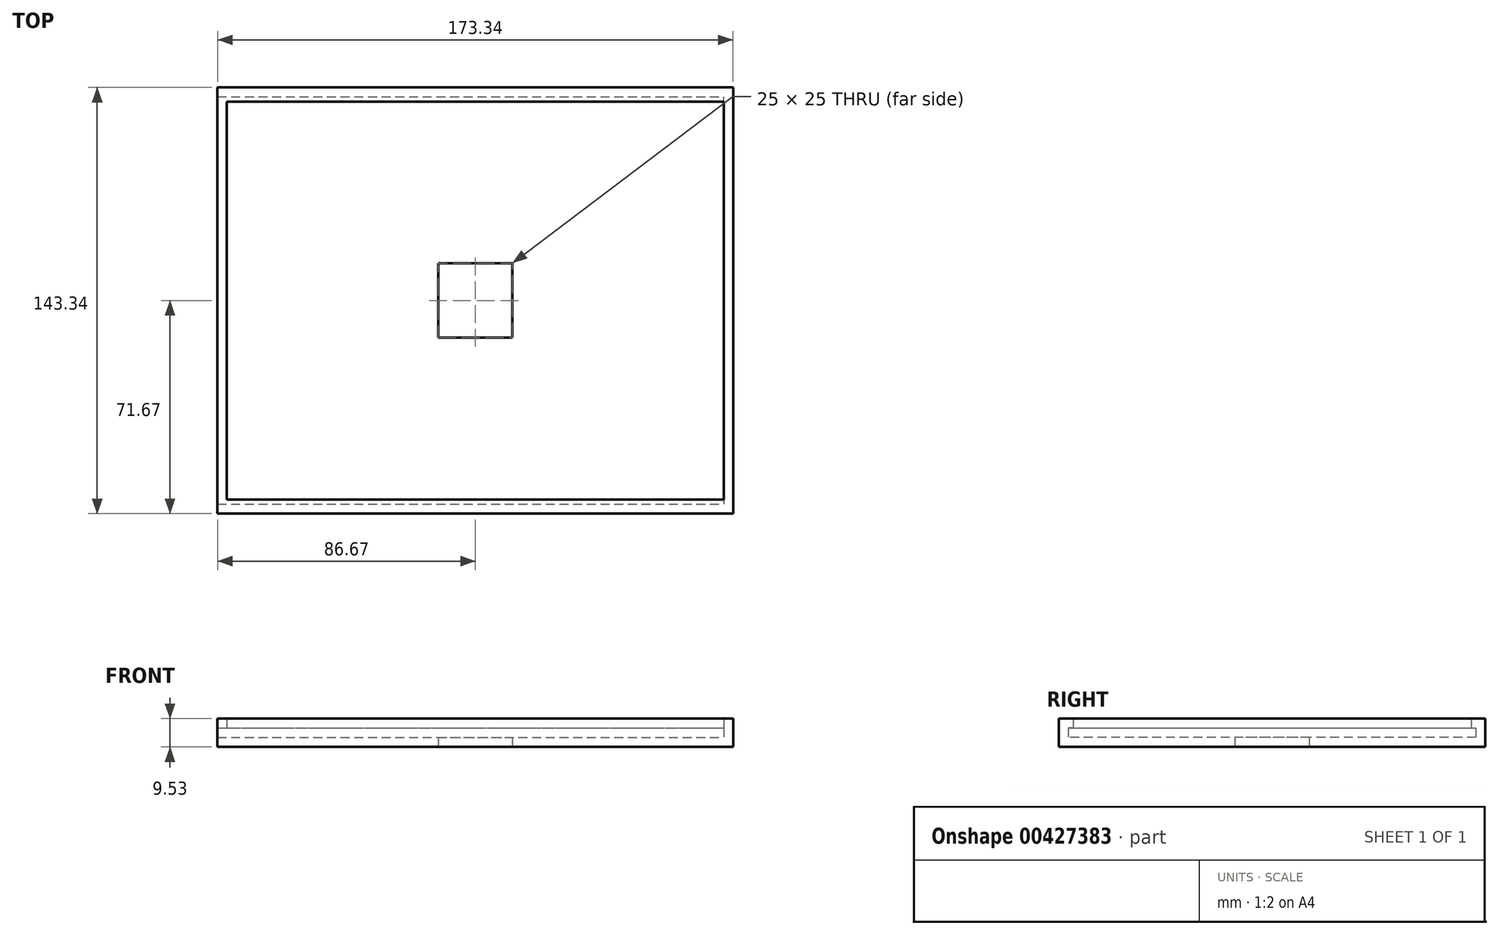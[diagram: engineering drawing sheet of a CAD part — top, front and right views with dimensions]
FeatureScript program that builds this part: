
annotation { "Feature Type Name" : "Feature", "Feature Type Description" : "" }
export const myFeature = defineFeature(function(context is Context, id is Id, definition is map)
    precondition{}
    {
        {
            var Q0;
            Q0=qCreatedBy(makeId("Top.planeOp"),FACE);
            var sketch = newSketch(context, id + "F0", { "sketchPlane" : qUnion([Q0])});
            skPoint(sketch, "E0.middle", {"position": v(0, 0) * mm});
            skLineSegment(sketch, "E1.bottom", {"start": v(-67.1, 68.5) * mm, "end": v(-41.7, 68.5) * mm});
            skLineSegment(sketch, "E1.top", {"start": v(-67.1, -68.5) * mm, "end": v(-41.7, -68.5) * mm});
            skLineSegment(sketch, "E1.left", {"start": v(-83.5, 52.1) * mm, "end": v(-83.5, 26.7) * mm});
            skLineSegment(sketch, "E1.right", {"start": v(83.5, 52.1) * mm, "end": v(83.5, 26.7) * mm});
            skLineSegment(sketch, "E2.bottom", {"start": v(-12.5, 12.5) * mm, "end": v(12.5, 12.5) * mm});
            skLineSegment(sketch, "E2.top", {"start": v(-12.5, -12.5) * mm, "end": v(12.5, -12.5) * mm});
            skLineSegment(sketch, "E2.left", {"start": v(-12.5, 12.5) * mm, "end": v(-12.5, -12.5) * mm});
            skLineSegment(sketch, "E2.right", {"start": v(12.5, 12.5) * mm, "end": v(12.5, -12.5) * mm});
            skLineSegment(sketch, "E3.trimOffspring", {"start": v(-83.5, -24.1) * mm, "end": v(-83.5, -49.5) * mm});
            skLineSegment(sketch, "E4.trimOffspring", {"start": v(34.5, -68.5) * mm, "end": v(59.9, -68.5) * mm});
            skLineSegment(sketch, "E5.trimOffspring", {"start": v(83.5, -24.1) * mm, "end": v(83.5, -49.5) * mm});
            skLineSegment(sketch, "E6.trimOffspring", {"start": v(34.5, 68.5) * mm, "end": v(59.9, 68.5) * mm});
            skLineSegment(sketch, "E7.trimOffspring", {"start": v(-16.3, 68.5) * mm, "end": v(9.1, 68.5) * mm});
            skLineSegment(sketch, "E8", {"start": v(-16.3, -68.5) * mm, "end": v(9.1, -68.5) * mm});
            skLineSegment(sketch, "E9", {"start": v(-83.5, 52.1) * mm, "end": v(-83.5, 68.5) * mm});
            skLineSegment(sketch, "E10", {"start": v(-83.5, 68.5) * mm, "end": v(-67.1, 68.5) * mm});
            skLineSegment(sketch, "E11", {"start": v(-41.7, 68.5) * mm, "end": v(-16.3, 68.5) * mm});
            skLineSegment(sketch, "E12", {"start": v(9.1, 68.5) * mm, "end": v(34.5, 68.5) * mm});
            skLineSegment(sketch, "E13", {"start": v(59.9, 68.5) * mm, "end": v(83.5, 68.5) * mm});
            skLineSegment(sketch, "E14", {"start": v(83.5, 68.5) * mm, "end": v(83.5, 52.1) * mm});
            skLineSegment(sketch, "E15", {"start": v(83.5, -24.1) * mm, "end": v(83.5, 26.7) * mm});
            skLineSegment(sketch, "E16", {"start": v(83.5, -49.5) * mm, "end": v(83.5, -68.5) * mm});
            skLineSegment(sketch, "E17", {"start": v(83.5, -68.5) * mm, "end": v(59.9, -68.5) * mm});
            skLineSegment(sketch, "E18", {"start": v(34.5, -68.5) * mm, "end": v(9.1, -68.5) * mm});
            skLineSegment(sketch, "E19", {"start": v(-16.3, -68.5) * mm, "end": v(-41.7, -68.5) * mm});
            skLineSegment(sketch, "E20", {"start": v(-83.5, -49.5) * mm, "end": v(-83.5, -68.5) * mm});
            skLineSegment(sketch, "E21", {"start": v(-83.5, -68.5) * mm, "end": v(-67.1, -68.5) * mm});
            skLineSegment(sketch, "E22", {"start": v(-83.5, -24.1) * mm, "end": v(-83.5, 26.7) * mm});
            skLineSegment(sketch, "E23.bottom", {"start": v(-86.68, 71.67) * mm, "end": v(86.68, 71.67) * mm});
            skLineSegment(sketch, "E23.top", {"start": v(-86.68, -71.67) * mm, "end": v(86.68, -71.67) * mm});
            skLineSegment(sketch, "E23.left", {"start": v(-86.68, 71.67) * mm, "end": v(-86.68, -71.67) * mm});
            skLineSegment(sketch, "E23.right", {"start": v(86.68, 71.67) * mm, "end": v(86.68, -71.67) * mm});
            skSolve(sketch);
        }
        {
            var Q0;
            Q0=makeQuery(id+"F0.imprint","IMPRINT",FACE,{"disambiguationData":[TD([[makeQuery(id+"F0.imprint","IMPRINT",EDGE,{"derivedFrom":sQuery(id+"F0.wireOp",EDGE,"E1.bottom")}),-1.0]])]});
            extrude(context, id + "F1", {"entities" : qUnion([Q0]), "depth" : 3.17 * mm, "offsetDistance" : 25.4 * mm});
        }
        {
            var Q0;
            Q0 = qSketchRegion(id + "F0", true);
            extrude(context, id + "F2", {"entities" : qUnion([Q0]), "operationType" : NewBodyOperationType.ADD, "depth" : 9.52 * mm});
        }
        {
            var Q0;
            Q0=makeQuery(id+"F2.opExtrude","SWEPT_FACE",FACE,{"disambiguationData":[OSD([sQuery(id+"F0.wireOp",EDGE,"E1.left"),sQuery(id+"F0.wireOp",EDGE,"E3.trimOffspring"),sQuery(id+"F0.wireOp",EDGE,"E9"),sQuery(id+"F0.wireOp",EDGE,"E20"),sQuery(id+"F0.wireOp",EDGE,"E22")])]});
            var sketch = newSketch(context, id + "F3", { "sketchPlane" : qUnion([Q0])});
            skLineSegment(sketch, "E24.bottom", {"start": v(-68.5, 6.35) * mm, "end": v(68.5, 6.35) * mm});
            skLineSegment(sketch, "E24.top", {"start": v(-68.5, 3.18) * mm, "end": v(68.5, 3.18) * mm});
            skLineSegment(sketch, "E24.left", {"start": v(-68.5, 6.35) * mm, "end": v(-68.5, 3.18) * mm});
            skLineSegment(sketch, "E24.right", {"start": v(68.5, 6.35) * mm, "end": v(68.5, 3.18) * mm});
            skSolve(sketch);
        }
        {
            var Q0;
            Q0=makeQuery(id+"F3.imprint","IMPRINT",FACE,{"disambiguationData":[TD([[makeQuery(id+"F3.imprint","IMPRINT",EDGE,{"derivedFrom":sQuery(id+"F3.wireOp",EDGE,"E24.bottom")}),-1.0]])]});
            extrude(context, id + "F4", {"entities" : qUnion([Q0]), "operationType" : NewBodyOperationType.REMOVE, "oppositeDirection" : true, "depth" : 25.4 * mm, "offsetDistance" : 25.4 * mm});
        }
        {
            var Q0;
            Q0=makeQuery(id+"F4.boolean.opBoolean","MERGE",FACE,{"derivedFrom":[makeQuery(id+"F2.opExtrude","SWEPT_FACE",FACE,{"disambiguationData":[OSD([sQuery(id+"F0.wireOp",EDGE,"E1.bottom"),sQuery(id+"F0.wireOp",EDGE,"E6.trimOffspring"),sQuery(id+"F0.wireOp",EDGE,"E7.trimOffspring"),sQuery(id+"F0.wireOp",EDGE,"E10"),sQuery(id+"F0.wireOp",EDGE,"E11"),sQuery(id+"F0.wireOp",EDGE,"E12"),sQuery(id+"F0.wireOp",EDGE,"E13")])]}),makeQuery(id+"F4.opExtrude","SWEPT_FACE",FACE,{"disambiguationData":[OSD([sQuery(id+"F3.wireOp",EDGE,"E24.right")])]})]});
            var sketch = newSketch(context, id + "F5", { "sketchPlane" : qUnion([Q0])});
            skLineSegment(sketch, "E25.bottom", {"start": v(-83.5, 9.53) * mm, "end": v(83.5, 9.53) * mm});
            skLineSegment(sketch, "E25.top", {"start": v(-83.5, 6.35) * mm, "end": v(83.5, 6.35) * mm});
            skLineSegment(sketch, "E25.left", {"start": v(-83.5, 9.53) * mm, "end": v(-83.5, 6.35) * mm});
            skLineSegment(sketch, "E25.right", {"start": v(83.5, 9.53) * mm, "end": v(83.5, 6.35) * mm});
            skSolve(sketch);
        }
        {
            var Q0;
            Q0 = qSketchRegion(id + "F5", true);
            extrude(context, id + "F6", {"entities" : qUnion([Q0]), "operationType" : NewBodyOperationType.ADD, "depth" : 1.59 * mm});
        }
        {
            var Q0;
            Q0=makeQuery(id+"F4.boolean.opBoolean","MERGE",FACE,{"derivedFrom":[makeQuery(id+"F2.opExtrude","SWEPT_FACE",FACE,{"disambiguationData":[OSD([sQuery(id+"F0.wireOp",EDGE,"E1.top"),sQuery(id+"F0.wireOp",EDGE,"E4.trimOffspring"),sQuery(id+"F0.wireOp",EDGE,"E8"),sQuery(id+"F0.wireOp",EDGE,"E17"),sQuery(id+"F0.wireOp",EDGE,"E18"),sQuery(id+"F0.wireOp",EDGE,"E19"),sQuery(id+"F0.wireOp",EDGE,"E21")])]}),makeQuery(id+"F4.opExtrude","SWEPT_FACE",FACE,{"disambiguationData":[OSD([sQuery(id+"F3.wireOp",EDGE,"E24.left")])]})]});
            var sketch = newSketch(context, id + "F7", { "sketchPlane" : qUnion([Q0])});
            skLineSegment(sketch, "E26.bottom", {"start": v(-83.5, 6.35) * mm, "end": v(83.5, 6.35) * mm});
            skLineSegment(sketch, "E26.top", {"start": v(-83.5, 9.53) * mm, "end": v(83.5, 9.53) * mm});
            skLineSegment(sketch, "E26.left", {"start": v(-83.5, 6.35) * mm, "end": v(-83.5, 9.53) * mm});
            skLineSegment(sketch, "E26.right", {"start": v(83.5, 6.35) * mm, "end": v(83.5, 9.53) * mm});
            skSolve(sketch);
        }
        {
            var Q0;
            Q0 = qSketchRegion(id + "F7", true);
            extrude(context, id + "F8", {"entities" : qUnion([Q0]), "operationType" : NewBodyOperationType.ADD, "depth" : 1.59 * mm});
        }
    });
